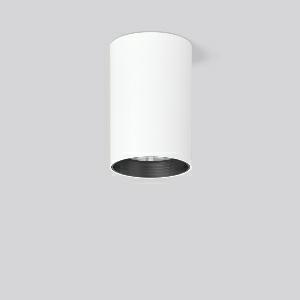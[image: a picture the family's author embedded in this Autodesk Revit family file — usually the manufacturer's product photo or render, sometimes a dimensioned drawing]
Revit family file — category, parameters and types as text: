
# Revit family: heledon_maxi_a_931221_002_2_84db
name_source: partatom
category: Lighting Fixtures
units: mm (PartAtom-declared; Revit-internal decimal feet)

## family parameters
Cut with Voids When Loaded = No
Host = Face
Light Source = No
Part Type = Normal
Room Calculation Point = No
Round Connector Dimension = Use Diameter
Shared = No

## types (1)
- HELEDON maxi A (1 x LED Modul 927, 2550 lm, 2700)
    Apparent Load = 25 VA
    Approval mark = CE
    CIE Flux Codes = 96 100 100 100 100
    Color Rendering = 92
    Color Temperature = 2700
    Default Elevation = 1800 mm
    Description = Series: HELEDON maxi
Cylindrical surface-mounted downlight. Housing: die-cast aluminium, powder-coated. Internal ceiling frame polycarbonate with bayonet mounting. Black plastic ring and recessed LED to prevent glare from the side. Optical assembly with lens made of plastic (polycarbonate) for the best homogeneous light distribution - can be changed without tools. Best colour rendering index Ra>90. Suitable for Ceiling mounting. Easy installation with a separate ceiling frame with bayonet mounting and plug connection. Driver integrated. Connected via plug-in connector. High quality converter without flickering and stroboscopic effect. The following accessories can be mounted without use of tools: interchangeable lenses, decorative glasses, honeycomb louvre, clear and frosted diffusers, white interchangeable plastic ring. 
Colour: traffic white, matt (RAL 9016)
Diameter: 123 mm
Height: 183 mm
Lamp: LED
Socket: without socket
Colour temperature: 2700K
Colour rendering index (CRI): 92
System power: 25 W
Rated luminous flux: 2550 lm
Luminous efficiency: 102 lm/W
Control gear: Regulated power supply
Protection class: I
Type of protection: IP 20
    Height = 183 mm
    Lamp = 1 x LED Modul 927
    Lamp Light Flux = 2550 lm
    Lamp count = 1
    Length = 123 mm
    Lifetime = 50000 h
    Luminous efficacy = 102 lm/W
    Manufacturer = RZB
    ModVariant = No
    Model = 931221.002.2
    Mounting Place = Ceiling
    Mounting Type = Surface mounted
    Number of Poles = 1
    OnlyDefault = Yes
    Power Factor = 1
    Product Name = HELEDON maxi A
    Product group = Surface mounted downlights
    ProductGroupID = 302
    Protection Class = Protection class I
    Protection Degree = IP 20
    RLX_Detail_Level = 1
    RLX_Emergency_Light_Flux = 0 lm
    RLX_Emergency_Type = 0
    RLX_Emergency_Type_DB = No
    RlxData = <blob elided: 95389 chars, md5=03d5f230>
    Socket = socket
    Standby Power = 0 W
    System Light Flux = 2550 lm
    System Power = 25 W
    Type Comments = Product without accessories
    Type Image = 931193.002.jpg
    URL = http://relux.com
    VarID = ---
    Voltage = 230 V
    Voltage Range = 220-240 V
    Weight = 0.00 kg
    Width = 0 mm  [stored 0 ft]

note: [stored X ft] marks values corroborated as IEEE doubles in the binary element streams (Revit-internal decimal feet)

## geometry (parser evidence)
native form markers: Blend x4, Sweep x9
no freeform markers — native parametric forms only
